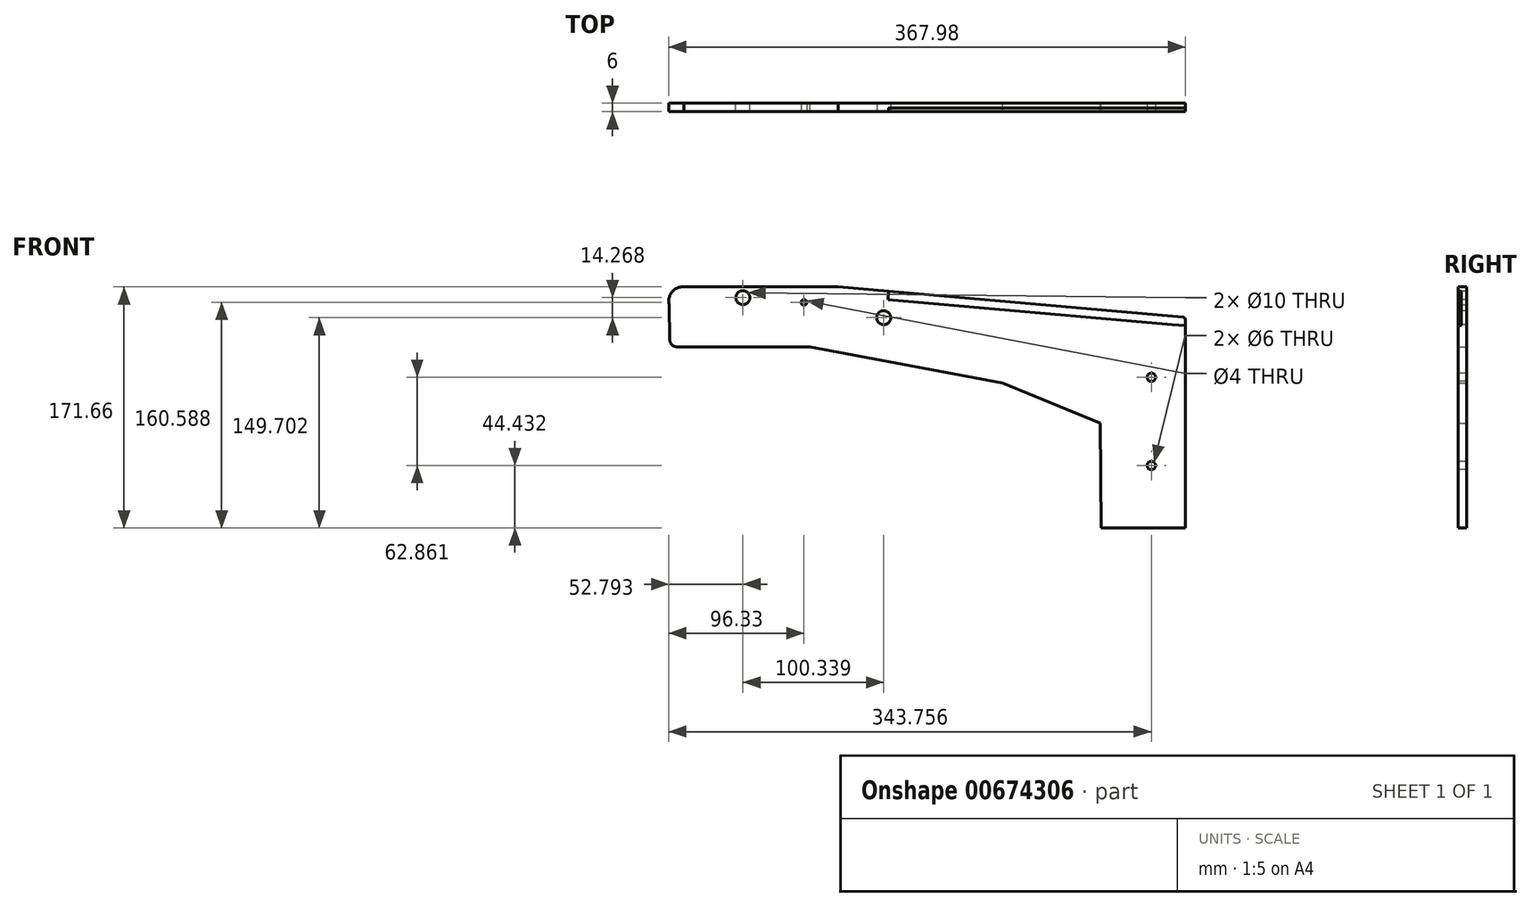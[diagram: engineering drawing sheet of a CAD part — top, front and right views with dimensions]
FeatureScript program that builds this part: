
annotation { "Feature Type Name" : "Feature", "Feature Type Description" : "" }
export const myFeature = defineFeature(function(context is Context, id is Id, definition is map)
    precondition{}
    {
        {
            var Q0;
            Q0=qCreatedBy(makeId("Front.planeOp"),FACE);
            var sketch = newSketch(context, id + "F0", { "sketchPlane" : qUnion([Q0])});
            skLineSegment(sketch, "E0", {"start": v(-49.9, 7.66) * mm, "end": v(60.1, 7.66) * mm});
            skArc(sketch, "E1", {"start": v(-49.9, 7.66) * mm, "mid": v(-58.4, 4) * mm, "end": v(-60.24, -5.07) * mm});
            skLineSegment(sketch, "E2", {"start": v(-49.93, -35) * mm, "end": v(40.07, -35) * mm});
            skLineSegment(sketch, "E3", {"start": v(307.35, -163.97) * mm, "end": v(247.35, -163.97) * mm});
            skLineSegment(sketch, "E4", {"start": v(-60.24, -5.07) * mm, "end": v(-59.88, -30.07) * mm});
            skLineSegment(sketch, "E5", {"start": v(-54.89, -35) * mm, "end": v(-49.93, -35) * mm});
            skPoint(sketch, "E6.visualSharp", {"position": v(-59.81, -35) * mm});
            skArc(sketch, "E6.filletArc", {"start": v(-59.88, -30.07) * mm, "mid": v(-58.4, -33.56) * mm, "end": v(-54.89, -35) * mm});
            skLineSegment(sketch, "E7", {"start": v(177.25, -60.95) * mm, "end": v(246.58, -89.53) * mm});
            skLineSegment(sketch, "E8", {"start": v(60.1, 7.66) * mm, "end": v(307.35, -13.97) * mm});
            skLineSegment(sketch, "E9", {"start": v(40.07, -35) * mm, "end": v(177.25, -60.95) * mm});
            skLineSegment(sketch, "E10", {"start": v(247.35, -163.97) * mm, "end": v(246.58, -89.53) * mm});
            skLineSegment(sketch, "E11", {"start": v(307.35, -163.97) * mm, "end": v(307.35, -13.97) * mm});
            skPoint(sketch, "E12.end.orphan", {"position": v(310.72, 0) * mm});
            skSolve(sketch);
        }
        {
            var Q0;
            Q0=qSketchRegion(id+"F0",true);
            extrude(context, id + "F1", {"entities" : qUnion([Q0]), "depth" : 6 * mm, "offsetDistance" : 25 * mm});
        }
        {
            var Q0;
            Q0=makeQuery(id+"F1.opExtrude","CAP_FACE",FACE,{"disambiguationData":[OSD([sQuery(id+"F0.wireOp",EDGE,"E0"),sQuery(id+"F0.wireOp",EDGE,"E1"),sQuery(id+"F0.wireOp",EDGE,"E2"),sQuery(id+"F0.wireOp",EDGE,"xIpO2BMK-1Sr3-U6kz-732z-lHFiZcdXaP95"),sQuery(id+"F0.wireOp",EDGE,"E3"),sQuery(id+"F0.wireOp",EDGE,"zyuM4KxI-rK7D-eBj5-RQWG-Z7kNhVQKbpSr"),sQuery(id+"F0.wireOp",EDGE,"E4"),sQuery(id+"F0.wireOp",EDGE,"E5"),sQuery(id+"F0.wireOp",EDGE,"E6.filletArc"),sQuery(id+"F0.wireOp",EDGE,"E7"),sQuery(id+"F0.wireOp",EDGE,"E8"),sQuery(id+"F0.wireOp",EDGE,"E9")])],"isStart":false});
            var sketch = newSketch(context, id + "F2", { "sketchPlane" : qUnion([Q0])});
            skLineSegment(sketch, "E13", {"start": v(-49.88, 0) * mm, "end": v(-60.37, 0) * mm});
            skLineSegment(sketch, "E14", {"start": v(-49.88, 0) * mm, "end": v(30.12, 0) * mm});
            skLineSegment(sketch, "E15", {"start": v(30.12, 0) * mm, "end": v(92.5, -8.77) * mm});
            skLineSegment(sketch, "E16", {"start": v(92.5, -8.77) * mm, "end": v(92.5, -14.27) * mm});
            skCircle(sketch, "E17", {"center": v(92.5, -14.27) * mm, "radius": 5 * mm});
            skSolve(sketch);
        }
        {
            var Q0;
            Q0=qSketchRegion(id+"F2",true);
            extrude(context, id + "F3", {"entities" : qUnion([Q0]), "operationType" : NewBodyOperationType.REMOVE, "endBound" : BoundingType.THROUGH_ALL, "oppositeDirection" : true, "depth" : 25 * mm, "offsetDistance" : 25 * mm});
        }
        {
            var Q0;
            Q0=makeQuery(id+"F1.opExtrude","CAP_FACE",FACE,{"disambiguationData":[OSD([sQuery(id+"F0.wireOp",EDGE,"E0"),sQuery(id+"F0.wireOp",EDGE,"E1"),sQuery(id+"F0.wireOp",EDGE,"E2"),sQuery(id+"F0.wireOp",EDGE,"xIpO2BMK-1Sr3-U6kz-732z-lHFiZcdXaP95"),sQuery(id+"F0.wireOp",EDGE,"E3"),sQuery(id+"F0.wireOp",EDGE,"zyuM4KxI-rK7D-eBj5-RQWG-Z7kNhVQKbpSr"),sQuery(id+"F0.wireOp",EDGE,"E4"),sQuery(id+"F0.wireOp",EDGE,"E5"),sQuery(id+"F0.wireOp",EDGE,"E6.filletArc"),sQuery(id+"F0.wireOp",EDGE,"E7"),sQuery(id+"F0.wireOp",EDGE,"E8"),sQuery(id+"F0.wireOp",EDGE,"E9")])],"isStart":false});
            var sketch = newSketch(context, id + "F4", { "sketchPlane" : qUnion([Q0])});
            skLineSegment(sketch, "E18", {"start": v(111.62, 3.16) * mm, "end": v(111.62, -8.84) * mm});
            skCircle(sketch, "E19", {"center": v(283.13, -119.54) * mm, "radius": 3 * mm});
            skCircle(sketch, "E20", {"center": v(283.13, -56.68) * mm, "radius": 3 * mm});
            skSolve(sketch);
        }
        {
            var Q0;
            Q0=qSketchRegion(id+"F4",true);
            extrude(context, id + "F5", {"entities" : qUnion([Q0]), "operationType" : NewBodyOperationType.REMOVE, "endBound" : BoundingType.THROUGH_ALL, "oppositeDirection" : true, "depth" : 25 * mm, "offsetDistance" : 25 * mm});
        }
        {
            var Q0;
            Q0=makeQuery(id+"F1.opExtrude","CAP_FACE",FACE,{"disambiguationData":[OSD([sQuery(id+"F0.wireOp",EDGE,"E0"),sQuery(id+"F0.wireOp",EDGE,"E1"),sQuery(id+"F0.wireOp",EDGE,"E2"),sQuery(id+"F0.wireOp",EDGE,"xIpO2BMK-1Sr3-U6kz-732z-lHFiZcdXaP95"),sQuery(id+"F0.wireOp",EDGE,"E3"),sQuery(id+"F0.wireOp",EDGE,"zyuM4KxI-rK7D-eBj5-RQWG-Z7kNhVQKbpSr"),sQuery(id+"F0.wireOp",EDGE,"E4"),sQuery(id+"F0.wireOp",EDGE,"E5"),sQuery(id+"F0.wireOp",EDGE,"E6.filletArc"),sQuery(id+"F0.wireOp",EDGE,"E7"),sQuery(id+"F0.wireOp",EDGE,"E8"),sQuery(id+"F0.wireOp",EDGE,"E9")])],"isStart":true});
            var sketch = newSketch(context, id + "F6", { "sketchPlane" : qUnion([Q0])});
            skCircle(sketch, "E21", {"center": v(7.84, 0) * mm, "radius": 5 * mm});
            skSolve(sketch);
        }
        {
            var Q0;
            Q0=qSketchRegion(id+"F6",true);
            extrude(context, id + "F7", {"entities" : qUnion([Q0]), "operationType" : NewBodyOperationType.REMOVE, "endBound" : BoundingType.THROUGH_ALL, "oppositeDirection" : true, "depth" : 25 * mm, "offsetDistance" : 25 * mm});
        }
        {
            var Q0;
            Q0=makeQuery(id+"F1.opExtrude","CAP_FACE",FACE,{"disambiguationData":[OSD([sQuery(id+"F0.wireOp",EDGE,"E0"),sQuery(id+"F0.wireOp",EDGE,"E1"),sQuery(id+"F0.wireOp",EDGE,"E2"),sQuery(id+"F0.wireOp",EDGE,"xIpO2BMK-1Sr3-U6kz-732z-lHFiZcdXaP95"),sQuery(id+"F0.wireOp",EDGE,"E3"),sQuery(id+"F0.wireOp",EDGE,"zyuM4KxI-rK7D-eBj5-RQWG-Z7kNhVQKbpSr"),sQuery(id+"F0.wireOp",EDGE,"E4"),sQuery(id+"F0.wireOp",EDGE,"E5"),sQuery(id+"F0.wireOp",EDGE,"E6.filletArc"),sQuery(id+"F0.wireOp",EDGE,"E7"),sQuery(id+"F0.wireOp",EDGE,"E8"),sQuery(id+"F0.wireOp",EDGE,"E9")])],"isStart":false});
            var sketch = newSketch(context, id + "F8", { "sketchPlane" : qUnion([Q0])});
            skCircle(sketch, "E22", {"center": v(35.7, -3.38) * mm, "radius": 2 * mm});
            skSolve(sketch);
        }
        {
            var Q0;
            Q0=qSketchRegion(id+"F8",true);
            extrude(context, id + "F9", {"entities" : qUnion([Q0]), "operationType" : NewBodyOperationType.REMOVE, "endBound" : BoundingType.THROUGH_ALL, "oppositeDirection" : true, "depth" : 25 * mm, "offsetDistance" : 25 * mm});
        }
        {
            var Q0;
            Q0=makeQuery(id+"F1.opExtrude","CAP_FACE",FACE,{"disambiguationData":[OSD([sQuery(id+"F0.wireOp",EDGE,"E0"),sQuery(id+"F0.wireOp",EDGE,"E1"),sQuery(id+"F0.wireOp",EDGE,"E2"),sQuery(id+"F0.wireOp",EDGE,"E3"),sQuery(id+"F0.wireOp",EDGE,"E4"),sQuery(id+"F0.wireOp",EDGE,"E5"),sQuery(id+"F0.wireOp",EDGE,"E6.filletArc"),sQuery(id+"F0.wireOp",EDGE,"E7"),sQuery(id+"F0.wireOp",EDGE,"E8"),sQuery(id+"F0.wireOp",EDGE,"E9"),sQuery(id+"F0.wireOp",EDGE,"E10"),sQuery(id+"F0.wireOp",EDGE,"E11")])],"isStart":false});
            var sketch = newSketch(context, id + "F10", { "sketchPlane" : qUnion([Q0])});
            skLineSegment(sketch, "E23", {"start": v(95.99, 4.53) * mm, "end": v(298.21, -13.17) * mm});
            skLineSegment(sketch, "E24", {"start": v(95.46, -1.45) * mm, "end": v(297.69, -19.14) * mm});
            skLineSegment(sketch, "E25", {"start": v(95.99, 4.53) * mm, "end": v(95.46, -1.45) * mm});
            skLineSegment(sketch, "E26", {"start": v(298.21, -13.17) * mm, "end": v(307.35, -13.97) * mm});
            skLineSegment(sketch, "E27", {"start": v(307.35, -13.97) * mm, "end": v(307.35, -19.97) * mm});
            skLineSegment(sketch, "E28", {"start": v(297.69, -19.14) * mm, "end": v(307.35, -19.97) * mm});
            skSolve(sketch);
        }
        {
            var Q0;
            Q0=qSketchRegion(id+"F10",true);
            extrude(context, id + "F11", {"entities" : qUnion([Q0]), "operationType" : NewBodyOperationType.REMOVE, "oppositeDirection" : true, "depth" : 2.5 * mm, "offsetDistance" : 25 * mm});
        }
        {
            var Q0;
            Q0=makeQuery(id+"F1.opExtrude","SWEPT_EDGE",EDGE,{"disambiguationData":[OSD([sQuery(id+"F0.wireOp",EDGE,"E8"),sQuery(id+"F0.wireOp",EDGE,"E11")])]});
            fillet(context, id + "F12", {"entities" : qUnion([Q0]), "radius" : 2 * mm, "tangentPropagation" : true, "allowEdgeOverflow" : false});
        }
    });
